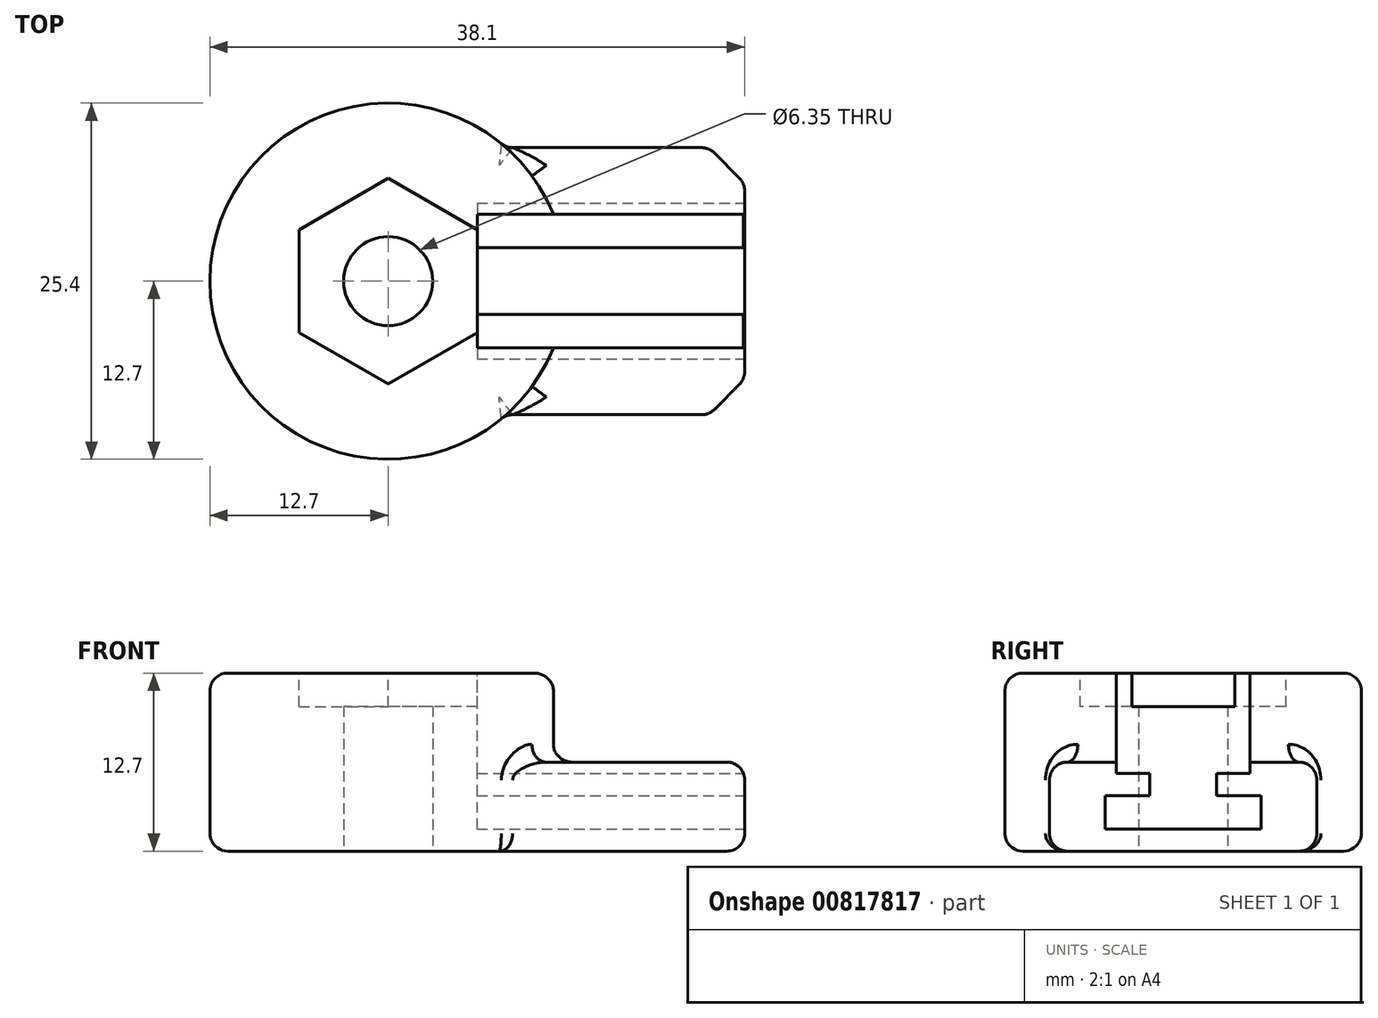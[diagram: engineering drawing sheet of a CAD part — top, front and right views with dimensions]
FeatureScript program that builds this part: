
annotation { "Feature Type Name" : "Feature", "Feature Type Description" : "" }
export const myFeature = defineFeature(function(context is Context, id is Id, definition is map)
    precondition{}
    {
        {
            var Q0;
            Q0=qCreatedBy(makeId("Top.planeOp"),FACE);
            var sketch = newSketch(context, id + "F0", { "sketchPlane" : qUnion([Q0])});
            skCircle(sketch, "E0", {"center": v(0, 0) * mm, "radius": 3.18 * mm});
            skCircle(sketch, "E1", {"center": v(0, 0) * mm, "radius": 12.7 * mm});
            skLineSegment(sketch, "E2.bottom", {"start": v(0, 9.53) * mm, "end": v(25.4, 9.53) * mm});
            skLineSegment(sketch, "E2.top", {"start": v(0, -9.52) * mm, "end": v(25.4, -9.52) * mm});
            skLineSegment(sketch, "E2.left", {"start": v(0, 9.52) * mm, "end": v(0, -9.52) * mm});
            skLineSegment(sketch, "E2.right", {"start": v(25.4, 9.52) * mm, "end": v(25.4, -9.52) * mm});
            skPoint(sketch, "E3", {"position": v(25.4, 0) * mm});
            skCircle(sketch, "E4.cCircle", {"center": v(0, 0) * mm, "radius": 7.33 * mm, "construction": true});
            skLineSegment(sketch, "E4.0", {"start": v(0, 7.33) * mm, "end": v(6.35, 3.67) * mm});
            skLineSegment(sketch, "E4.1", {"start": v(6.35, 3.67) * mm, "end": v(6.35, -3.67) * mm});
            skLineSegment(sketch, "E4.2", {"start": v(6.35, -3.67) * mm, "end": v(0, -7.33) * mm});
            skLineSegment(sketch, "E4.3", {"start": v(0, -7.33) * mm, "end": v(-6.35, -3.67) * mm});
            skLineSegment(sketch, "E4.4", {"start": v(-6.35, -3.67) * mm, "end": v(-6.35, 3.67) * mm});
            skLineSegment(sketch, "E4.5", {"start": v(-6.35, 3.67) * mm, "end": v(0, 7.33) * mm});
            skSolve(sketch);
        }
        {
            var Q0;
            {var subQ5=sQuery(id+"F0.wireOp",EDGE,"E2.right");Q0=makeQuery(id+"F0.imprint","IMPRINT",FACE,{"disambiguationData":[TD([[makeQuery(id+"F0.imprint","IMPRINT",EDGE,{"derivedFrom":subQ5}),-1.0]])]});}
            var Q1;
            {var subQ8=sQuery(id+"F0.wireOp",EDGE,"E4.3");Q1=makeQuery(id+"F0.imprint","IMPRINT",FACE,{"disambiguationData":[TD([[makeQuery(id+"F0.imprint","IMPRINT",EDGE,{"derivedFrom":subQ8}),1.0]])]});}
            var Q2;
            {var subQ8=sQuery(id+"F0.wireOp",EDGE,"E4.0");Q2=makeQuery(id+"F0.imprint","IMPRINT",FACE,{"disambiguationData":[TD([[makeQuery(id+"F0.imprint","IMPRINT",EDGE,{"derivedFrom":subQ8}),1.0]])]});}
            var Q3;
            {var subQ0=sQuery(id+"F0.wireOp",EDGE,"E4.3");Q3=makeQuery(id+"F0.imprint","IMPRINT",FACE,{"disambiguationData":[TD([[makeQuery(id+"F0.imprint","IMPRINT",EDGE,{"derivedFrom":subQ0}),-1.0]])]});}
            var Q4;
            {var subQ0=sQuery(id+"F0.wireOp",EDGE,"E4.0");Q4=makeQuery(id+"F0.imprint","IMPRINT",FACE,{"disambiguationData":[TD([[makeQuery(id+"F0.imprint","IMPRINT",EDGE,{"derivedFrom":subQ0}),-1.0]])]});}
            extrude(context, id + "F1", {"entities" : qUnion([Q0, Q1, Q2, Q3, Q4]), "depth" : 6.35 * mm, "offsetDistance" : 25.4 * mm});
        }
        {
            var Q0;
            Q0=qCreatedBy(makeId("Top.planeOp"),FACE);
            var sketch = newSketch(context, id + "F2", { "sketchPlane" : qUnion([Q0])});
            skCircle(sketch, "E5.0", {"center": v(0, 0) * mm, "radius": 12.7 * mm});
            skCircle(sketch, "E6.0", {"center": v(0, 0) * mm, "radius": 3.18 * mm});
            skSolve(sketch);
        }
        {
            var Q0;
            Q0 = qSketchRegion(id + "F2", true);
            extrude(context, id + "F3", {"entities" : qUnion([Q0]), "operationType" : NewBodyOperationType.ADD, "depth" : 12.7 * mm, "offsetDistance" : 25.4 * mm});
        }
        {
            var Q0;
            Q0=makeQuery(id+"F1.opExtrude","SWEPT_FACE",FACE,{"disambiguationData":[OSD([sQuery(id+"F0.wireOp",EDGE,"E2.right")])]});
            var sketch = newSketch(context, id + "F4", { "sketchPlane" : qUnion([Q0])});
            skPoint(sketch, "E7", {"position": v(0, 2.78) * mm});
            skLineSegment(sketch, "E8.bottom", {"start": v(5.56, 1.59) * mm, "end": v(-5.56, 1.59) * mm});
            skLineSegment(sketch, "E8.top", {"start": v(5.56, 3.97) * mm, "end": v(-5.56, 3.97) * mm});
            skLineSegment(sketch, "E8.left", {"start": v(5.56, 1.59) * mm, "end": v(5.56, 3.97) * mm});
            skLineSegment(sketch, "E8.right", {"start": v(-5.56, 1.59) * mm, "end": v(-5.56, 3.97) * mm});
            skLineSegment(sketch, "E9.bottom", {"start": v(-2.38, 3.97) * mm, "end": v(2.38, 3.97) * mm});
            skLineSegment(sketch, "E9.top", {"start": v(-2.38, 5.56) * mm, "end": v(2.38, 5.56) * mm});
            skLineSegment(sketch, "E9.left", {"start": v(-2.38, 3.97) * mm, "end": v(-2.38, 5.56) * mm});
            skLineSegment(sketch, "E9.right", {"start": v(2.38, 3.97) * mm, "end": v(2.38, 5.56) * mm});
            skPoint(sketch, "E10", {"position": v(0, 5.56) * mm});
            skLineSegment(sketch, "E11.bottom", {"start": v(-4.76, 5.56) * mm, "end": v(4.76, 5.56) * mm});
            skLineSegment(sketch, "E11.top", {"start": v(-4.76, 6.35) * mm, "end": v(4.76, 6.35) * mm});
            skLineSegment(sketch, "E11.left", {"start": v(-4.76, 5.56) * mm, "end": v(-4.76, 6.35) * mm});
            skLineSegment(sketch, "E11.right", {"start": v(4.76, 5.56) * mm, "end": v(4.76, 6.35) * mm});
            skPoint(sketch, "E12", {"position": v(0, 6.35) * mm});
            skLineSegment(sketch, "E13.0", {"start": v(-9.52, 6.35) * mm, "end": v(-9.52, 0) * mm, "construction": true});
            skPoint(sketch, "E14", {"position": v(-9.52, 3.18) * mm});
            skLineSegment(sketch, "E15.top", {"start": v(-4.76, 15.62) * mm, "end": v(4.76, 15.62) * mm});
            skLineSegment(sketch, "E15.left", {"start": v(-4.76, 6.35) * mm, "end": v(-4.76, 15.62) * mm});
            skLineSegment(sketch, "E15.right", {"start": v(4.76, 6.35) * mm, "end": v(4.76, 15.62) * mm});
            skSolve(sketch);
        }
        {
            var Q0;
            Q0=qSketchRegion(id+"F4",true);
            extrude(context, id + "F5", {"entities" : qUnion([Q0]), "operationType" : NewBodyOperationType.REMOVE, "oppositeDirection" : true, "depth" : 19.05 * mm, "offsetDistance" : 25.4 * mm});
        }
        {
            var Q0;
            Q0=makeQuery(id+"F3.opExtrude","CAP_FACE",FACE,{"disambiguationData":[OSD([sQuery(id+"F2.wireOp",EDGE,"E5.0"),sQuery(id+"F2.wireOp",EDGE,"E6.0")])],"isStart":false});
            var sketch = newSketch(context, id + "F6", { "sketchPlane" : qUnion([Q0])});
            skCircle(sketch, "E16.0", {"center": v(0, 0) * mm, "radius": 7.33 * mm, "construction": true});
            skLineSegment(sketch, "E17.0", {"start": v(-6.35, 3.67) * mm, "end": v(0, 7.33) * mm});
            skLineSegment(sketch, "E18.0", {"start": v(-6.35, -3.67) * mm, "end": v(-6.35, 3.67) * mm});
            skLineSegment(sketch, "E19.0", {"start": v(0, -7.33) * mm, "end": v(-6.35, -3.67) * mm});
            skLineSegment(sketch, "E20.0", {"start": v(6.35, -3.67) * mm, "end": v(0, -7.33) * mm});
            skLineSegment(sketch, "E21.0", {"start": v(6.35, 3.67) * mm, "end": v(6.35, -3.67) * mm});
            skLineSegment(sketch, "E22.0", {"start": v(0, 7.33) * mm, "end": v(6.35, 3.67) * mm});
            skSolve(sketch);
        }
        {
            var Q0;
            Q0 = qSketchRegion(id + "F6", true);
            extrude(context, id + "F7", {"entities" : qUnion([Q0]), "operationType" : NewBodyOperationType.REMOVE, "oppositeDirection" : true, "depth" : 2.38 * mm, "offsetDistance" : 25.4 * mm});
        }
        {
            var Q0;
            Q0=makeQuery(id+"F1.opExtrude","SWEPT_EDGE",EDGE,{"disambiguationData":[OSD([sQuery(id+"F0.wireOp",EDGE,"E2.bottom"),sQuery(id+"F0.wireOp",EDGE,"E2.right")])]});
            var Q1;
            Q1=makeQuery(id+"F1.opExtrude","SWEPT_EDGE",EDGE,{"disambiguationData":[OSD([sQuery(id+"F0.wireOp",EDGE,"E2.top"),sQuery(id+"F0.wireOp",EDGE,"E2.right")])]});
            chamfer(context, id + "F8", {"entities" : qUnion([Q0, Q1]), "width" : 2.54 * mm, "tangentPropagation" : true});
        }
        {
            var Q0;
            Q0=makeQuery(id+"F1.opExtrude","CAP_EDGE",EDGE,{"disambiguationData":[OSD([sQuery(id+"F0.wireOp",EDGE,"E2.top")])],"isStart":false});
            var Q1;
            Q1=makeQuery(id+"F1.opExtrude","CAP_EDGE",EDGE,{"disambiguationData":[OSD([sQuery(id+"F0.wireOp",EDGE,"E2.right")])],"isStart":false});
            var Q2;
            {var subQ0=sQuery(id+"F0.wireOp",EDGE,"E2.right");var subQ1=sQuery(id+"F0.wireOp",EDGE,"E2.top");Q2=makeQuery(id+"F8.opChamfer","BLEND_EDGE",EDGE,{"blendedFrom":[makeQuery(id+"F1.opExtrude","SWEPT_EDGE",EDGE,{"disambiguationData":[OSD([subQ1,subQ0])]}),makeQuery(id+"F1.opExtrude","CAP_FACE",FACE,{"disambiguationData":[OSD([sQuery(id+"F0.wireOp",EDGE,"E0"),sQuery(id+"F0.wireOp",EDGE,"E1"),sQuery(id+"F0.wireOp",EDGE,"E2.bottom"),subQ1,subQ0])],"isStart":false})],"blendedInto":[makeQuery(id+"F1.opExtrude","CAP_FACE",FACE,{"disambiguationData":[OSD([sQuery(id+"F0.wireOp",EDGE,"E0"),sQuery(id+"F0.wireOp",EDGE,"E1"),sQuery(id+"F0.wireOp",EDGE,"E2.bottom"),subQ1,subQ0])],"isStart":false})]});}
            var Q3;
            Q3=makeQuery(id+"F1.opExtrude","CAP_EDGE",EDGE,{"disambiguationData":[OSD([sQuery(id+"F0.wireOp",EDGE,"E1")])],"isStart":false});
            var Q4;
            {var subQ0=sQuery(id+"F0.wireOp",EDGE,"E2.right");var subQ1=sQuery(id+"F0.wireOp",EDGE,"E2.bottom");Q4=makeQuery(id+"F8.opChamfer","BLEND_EDGE",EDGE,{"blendedFrom":[makeQuery(id+"F1.opExtrude","SWEPT_EDGE",EDGE,{"disambiguationData":[OSD([subQ1,subQ0])]}),makeQuery(id+"F1.opExtrude","CAP_FACE",FACE,{"disambiguationData":[OSD([sQuery(id+"F0.wireOp",EDGE,"E0"),sQuery(id+"F0.wireOp",EDGE,"E1"),subQ1,sQuery(id+"F0.wireOp",EDGE,"E2.top"),subQ0])],"isStart":false})],"blendedInto":[makeQuery(id+"F1.opExtrude","CAP_FACE",FACE,{"disambiguationData":[OSD([sQuery(id+"F0.wireOp",EDGE,"E0"),sQuery(id+"F0.wireOp",EDGE,"E1"),subQ1,sQuery(id+"F0.wireOp",EDGE,"E2.top"),subQ0])],"isStart":false})]});}
            var Q5;
            Q5=makeQuery(id+"F1.opExtrude","CAP_EDGE",EDGE,{"disambiguationData":[OSD([sQuery(id+"F0.wireOp",EDGE,"E2.bottom")])],"isStart":false});
            var Q6;
            {var subQ0=sQuery(id+"F0.wireOp",EDGE,"E2.right");var subQ1=sQuery(id+"F0.wireOp",EDGE,"E2.bottom");Q6=makeQuery(id+"F8.opChamfer","BLEND_EDGE",EDGE,{"blendedFrom":[makeQuery(id+"F1.opExtrude","SWEPT_EDGE",EDGE,{"disambiguationData":[OSD([subQ1,subQ0])]}),makeQuery(id+"F1.opExtrude","CAP_FACE",FACE,{"disambiguationData":[OSD([sQuery(id+"F0.wireOp",EDGE,"E0"),sQuery(id+"F0.wireOp",EDGE,"E1"),subQ1,sQuery(id+"F0.wireOp",EDGE,"E2.top"),subQ0])],"isStart":true})],"blendedInto":[makeQuery(id+"F1.opExtrude","CAP_FACE",FACE,{"disambiguationData":[OSD([sQuery(id+"F0.wireOp",EDGE,"E0"),sQuery(id+"F0.wireOp",EDGE,"E1"),subQ1,sQuery(id+"F0.wireOp",EDGE,"E2.top"),subQ0])],"isStart":true})]});}
            var Q7;
            Q7=makeQuery(id+"F1.opExtrude","CAP_EDGE",EDGE,{"disambiguationData":[OSD([sQuery(id+"F0.wireOp",EDGE,"E2.bottom")])],"isStart":true});
            var Q8;
            Q8=makeQuery(id+"F1.opExtrude","CAP_EDGE",EDGE,{"disambiguationData":[OSD([sQuery(id+"F0.wireOp",EDGE,"E1")])],"isStart":true});
            var Q9;
            Q9=makeQuery(id+"F1.opExtrude","CAP_EDGE",EDGE,{"disambiguationData":[OSD([sQuery(id+"F0.wireOp",EDGE,"E2.right")])],"isStart":true});
            var Q10;
            {var subQ0=sQuery(id+"F0.wireOp",EDGE,"E2.right");var subQ1=sQuery(id+"F0.wireOp",EDGE,"E2.top");Q10=makeQuery(id+"F8.opChamfer","BLEND_EDGE",EDGE,{"blendedFrom":[makeQuery(id+"F1.opExtrude","SWEPT_EDGE",EDGE,{"disambiguationData":[OSD([subQ1,subQ0])]}),makeQuery(id+"F1.opExtrude","CAP_FACE",FACE,{"disambiguationData":[OSD([sQuery(id+"F0.wireOp",EDGE,"E0"),sQuery(id+"F0.wireOp",EDGE,"E1"),sQuery(id+"F0.wireOp",EDGE,"E2.bottom"),subQ1,subQ0])],"isStart":true})],"blendedInto":[makeQuery(id+"F1.opExtrude","CAP_FACE",FACE,{"disambiguationData":[OSD([sQuery(id+"F0.wireOp",EDGE,"E0"),sQuery(id+"F0.wireOp",EDGE,"E1"),sQuery(id+"F0.wireOp",EDGE,"E2.bottom"),subQ1,subQ0])],"isStart":true})]});}
            var Q11;
            Q11=makeQuery(id+"F1.opExtrude","CAP_EDGE",EDGE,{"disambiguationData":[OSD([sQuery(id+"F0.wireOp",EDGE,"E2.top")])],"isStart":true});
            var Q12;
            Q12=makeQuery(id+"F3.opExtrude","CAP_EDGE",EDGE,{"disambiguationData":[OSD([sQuery(id+"F2.wireOp",EDGE,"E5.0")])],"isStart":false});
            fillet(context, id + "F9", {"entities" : qUnion([Q0, Q1, Q2, Q3, Q4, Q5, Q6, Q7, Q8, Q9, Q10, Q11, Q12]), "radius" : 1.27 * mm, "tangentPropagation" : true, "allowEdgeOverflow" : false});
        }
        {
            var Q0;
            Q0=makeQuery(id+"F1.opExtrude","SWEPT_EDGE",EDGE,{"disambiguationData":[OSD([sQuery(id+"F0.wireOp",EDGE,"E1"),sQuery(id+"F0.wireOp",EDGE,"E2.bottom")])]});
            var Q1;
            {var subQ0=sQuery(id+"F0.wireOp",EDGE,"E2.bottom");Q1=makeQuery(id+"F8.opChamfer","BLEND_EDGE",EDGE,{"blendedFrom":[makeQuery(id+"F1.opExtrude","SWEPT_EDGE",EDGE,{"disambiguationData":[OSD([subQ0,sQuery(id+"F0.wireOp",EDGE,"E2.right")])]}),makeQuery(id+"F1.opExtrude","SWEPT_FACE",FACE,{"disambiguationData":[OSD([subQ0])]})],"blendedInto":[makeQuery(id+"F1.opExtrude","SWEPT_FACE",FACE,{"disambiguationData":[OSD([subQ0])]})]});}
            var Q2;
            Q2=makeQuery(id+"F1.opExtrude","SWEPT_EDGE",EDGE,{"disambiguationData":[OSD([sQuery(id+"F0.wireOp",EDGE,"E1"),sQuery(id+"F0.wireOp",EDGE,"E2.top")])]});
            var Q3;
            {var subQ0=sQuery(id+"F0.wireOp",EDGE,"E2.top");Q3=makeQuery(id+"F8.opChamfer","BLEND_EDGE",EDGE,{"blendedFrom":[makeQuery(id+"F1.opExtrude","SWEPT_EDGE",EDGE,{"disambiguationData":[OSD([subQ0,sQuery(id+"F0.wireOp",EDGE,"E2.right")])]}),makeQuery(id+"F1.opExtrude","SWEPT_FACE",FACE,{"disambiguationData":[OSD([subQ0])]})],"blendedInto":[makeQuery(id+"F1.opExtrude","SWEPT_FACE",FACE,{"disambiguationData":[OSD([subQ0])]})]});}
            var Q4;
            {var subQ0=sQuery(id+"F0.wireOp",EDGE,"E2.right");Q4=makeQuery(id+"F8.opChamfer","BLEND_EDGE",EDGE,{"blendedFrom":[makeQuery(id+"F1.opExtrude","SWEPT_EDGE",EDGE,{"disambiguationData":[OSD([sQuery(id+"F0.wireOp",EDGE,"E2.bottom"),subQ0])]}),makeQuery(id+"F1.opExtrude","SWEPT_FACE",FACE,{"disambiguationData":[OSD([subQ0])]})],"blendedInto":[makeQuery(id+"F1.opExtrude","SWEPT_FACE",FACE,{"disambiguationData":[OSD([subQ0])]})]});}
            var Q5;
            {var subQ0=sQuery(id+"F0.wireOp",EDGE,"E2.right");Q5=makeQuery(id+"F8.opChamfer","BLEND_EDGE",EDGE,{"blendedFrom":[makeQuery(id+"F1.opExtrude","SWEPT_EDGE",EDGE,{"disambiguationData":[OSD([sQuery(id+"F0.wireOp",EDGE,"E2.top"),subQ0])]}),makeQuery(id+"F1.opExtrude","SWEPT_FACE",FACE,{"disambiguationData":[OSD([subQ0])]})],"blendedInto":[makeQuery(id+"F1.opExtrude","SWEPT_FACE",FACE,{"disambiguationData":[OSD([subQ0])]})]});}
            fillet(context, id + "F10", {"entities" : qUnion([Q0, Q1, Q2, Q3, Q4, Q5]), "radius" : 1.27 * mm, "tangentPropagation" : true, "allowEdgeOverflow" : false});
        }
    });
